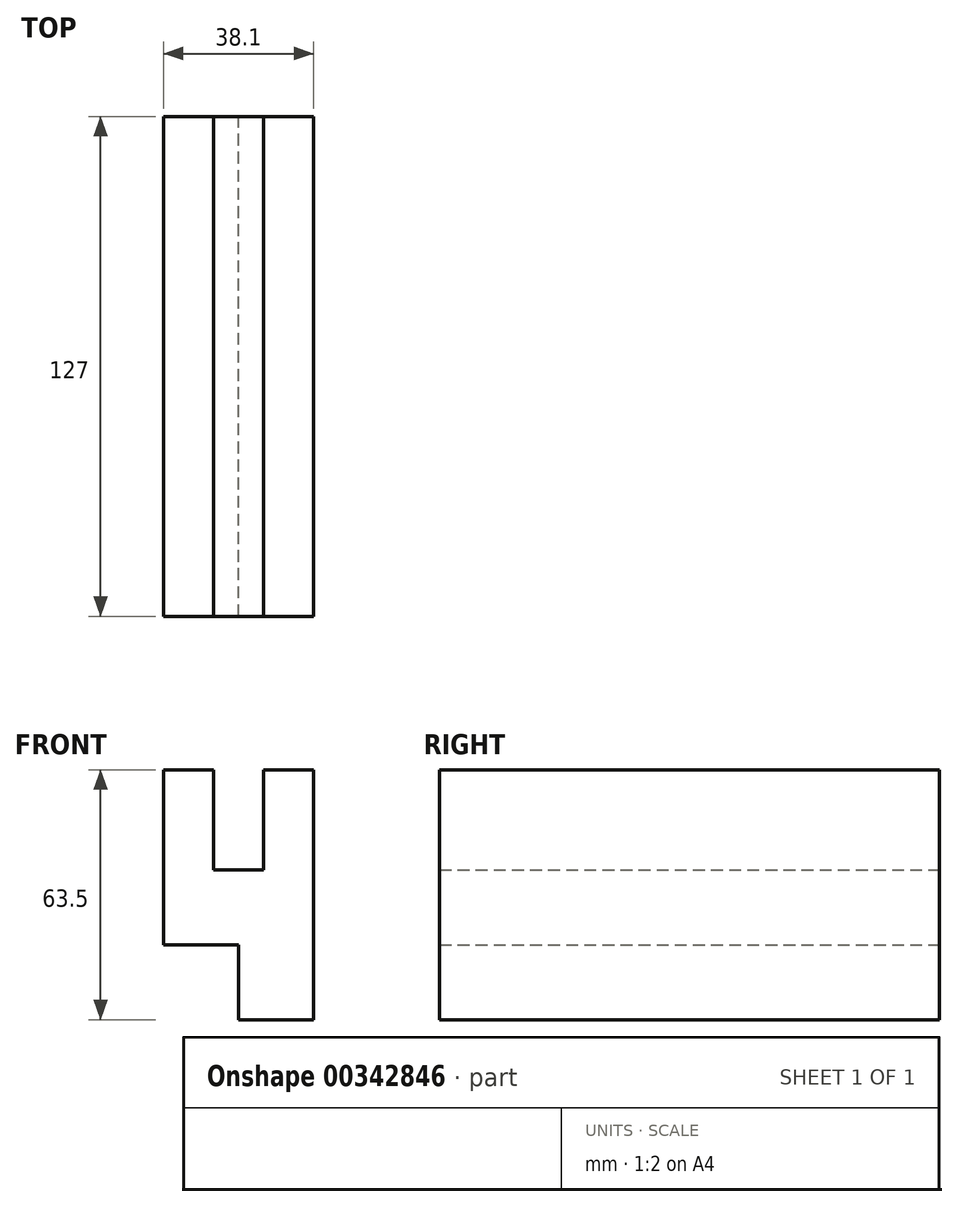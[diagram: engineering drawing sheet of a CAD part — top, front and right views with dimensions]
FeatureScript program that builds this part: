
annotation { "Feature Type Name" : "Feature", "Feature Type Description" : "" }
export const myFeature = defineFeature(function(context is Context, id is Id, definition is map)
    precondition{}
    {
        {
            var Q0;
            Q0=qCreatedBy(makeId("Front.planeOp"),FACE);
            var sketch = newSketch(context, id + "F0", { "sketchPlane" : qUnion([Q0])});
            skLineSegment(sketch, "E0.bottom", {"start": v(19.05, -31.75) * mm, "end": v(0, -31.75) * mm});
            skLineSegment(sketch, "E0.top", {"start": v(19.05, 31.75) * mm, "end": v(6.35, 31.75) * mm});
            skLineSegment(sketch, "E0.left", {"start": v(19.05, -31.75) * mm, "end": v(19.05, 31.75) * mm});
            skLineSegment(sketch, "E0.right", {"start": v(-19.05, -12.7) * mm, "end": v(-19.05, 31.75) * mm});
            skPoint(sketch, "E0.middle", {"position": v(0, 0) * mm});
            skLineSegment(sketch, "E1", {"start": v(-19.05, 31.75) * mm, "end": v(-6.35, 31.75) * mm});
            skLineSegment(sketch, "E2", {"start": v(-19.05, 31.75) * mm, "end": v(-19.05, 6.35) * mm});
            skLineSegment(sketch, "E3", {"start": v(-6.35, 31.75) * mm, "end": v(-6.35, 6.35) * mm});
            skLineSegment(sketch, "E4", {"start": v(-6.35, 6.35) * mm, "end": v(6.35, 6.35) * mm});
            skLineSegment(sketch, "E5", {"start": v(6.35, 6.35) * mm, "end": v(6.35, 31.75) * mm});
            skLineSegment(sketch, "E6", {"start": v(-19.05, -12.7) * mm, "end": v(0, -12.7) * mm});
            skLineSegment(sketch, "E7", {"start": v(0, -12.7) * mm, "end": v(0, -31.75) * mm});
            skPoint(sketch, "E8.orphan", {"position": v(-19.05, -31.75) * mm});
            skLineSegment(sketch, "E9.trimOffspring", {"start": v(-6.35, 31.75) * mm, "end": v(-19.05, 31.75) * mm});
            skSolve(sketch);
        }
        {
            var Q0;
            Q0 = qSketchRegion(id + "F0", true);
            extrude(context, id + "F1", {"entities" : qUnion([Q0]), "depth" : 127 * mm});
        }
    });
